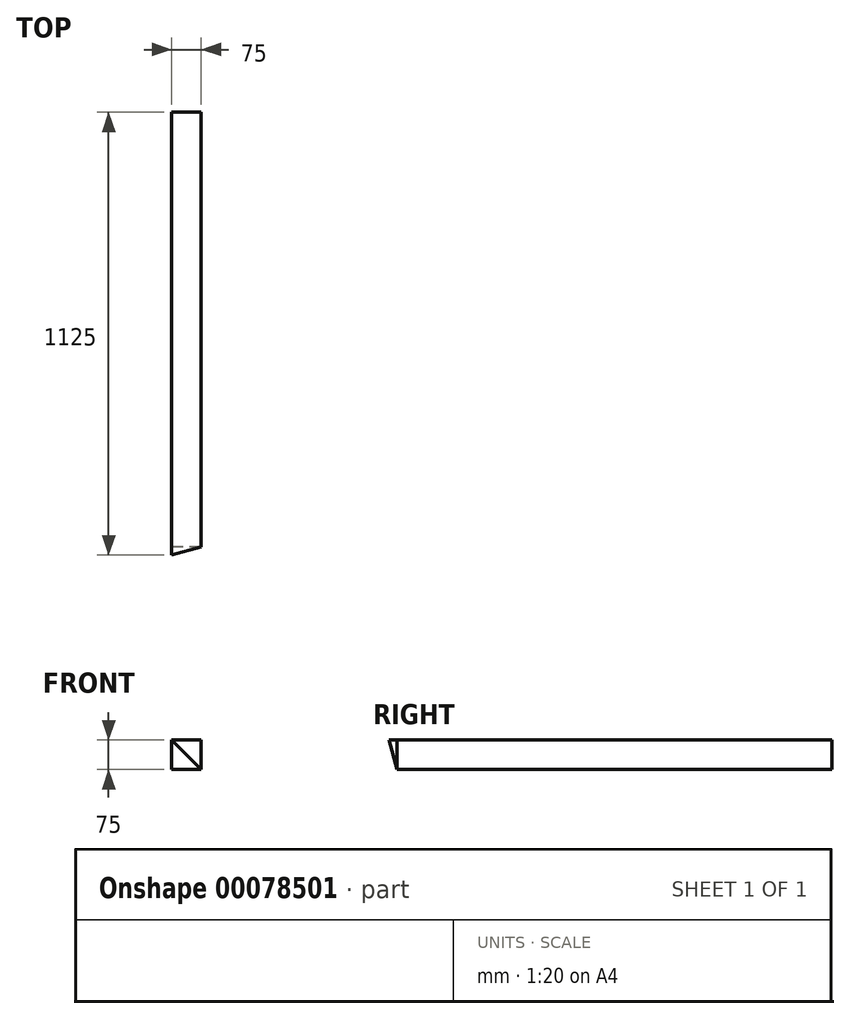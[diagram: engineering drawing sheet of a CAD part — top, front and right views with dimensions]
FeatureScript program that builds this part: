
annotation { "Feature Type Name" : "Feature", "Feature Type Description" : "" }
export const myFeature = defineFeature(function(context is Context, id is Id, definition is map)
    precondition{}
    {
        {
            var Q0;
            Q0=qCreatedBy(makeId("Front.planeOp"),FACE);
            var sketch = newSketch(context, id + "F0", { "sketchPlane" : qUnion([Q0])});
            skLineSegment(sketch, "E0.bottom", {"start": v(37.5, -37.5) * mm, "end": v(-37.5, -37.5) * mm});
            skLineSegment(sketch, "E0.top", {"start": v(37.5, 37.5) * mm, "end": v(-37.5, 37.5) * mm});
            skLineSegment(sketch, "E0.left", {"start": v(37.5, -37.5) * mm, "end": v(37.5, 37.5) * mm});
            skLineSegment(sketch, "E0.right", {"start": v(-37.5, -37.5) * mm, "end": v(-37.5, 37.5) * mm});
            skPoint(sketch, "E0.middle", {"position": v(0, 0) * mm});
            skSolve(sketch);
        }
        {
            var Q0;
            Q0 = qSketchRegion(id + "F0", true);
            extrude(context, id + "F1", {"entities" : qUnion([Q0]), "depth" : 1125 * mm});
        }
        {
            var Q0;
            Q0=makeQuery(id+"F1.opExtrude","CAP_EDGE",EDGE,{"disambiguationData":[OSD([sQuery(id+"F0.wireOp",EDGE,"E0.left")])],"isStart":false});
            var Q1;
            Q1=makeQuery(id+"F1.opExtrude","CAP_EDGE",EDGE,{"disambiguationData":[OSD([sQuery(id+"F0.wireOp",EDGE,"E0.bottom")])],"isStart":false});
            chamfer(context, id + "F2", {"entities" : qUnion([Q0, Q1]), "chamferType" : ChamferType.OFFSET_ANGLE, "width" : 75 * mm, "oppositeDirection" : false, "angle" : 15 * degree, "tangentPropagation" : true});
        }
    });
